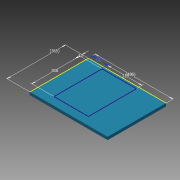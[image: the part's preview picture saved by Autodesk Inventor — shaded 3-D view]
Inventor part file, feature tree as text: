
AUTODESK INVENTOR PART (.ipt)
format: ipt  version: 2013 SP2 (Build 170200200, 200)  size: 77,312 bytes
history: native  units: mm
features: sketch x2, extrude x1
ambient origin geometry x8: Origin, YZ Plane, XZ Plane, XY Plane, X Axis, Y Axis, Z Axis, Center Point
bodies: Solid1 (feature_tree)
feature tree (3):
  extrude  "Extrusion1"  Depth=365.0mm
  sketch  "Sketch2"  dims[d2=18.0mm d3=0.0mm d4=300.0mm d6=215.0mm d7=15.0mm d8=100.0mm d9=486.0mm d10=365.0mm]
  sketch  "Sketch1"  dims[d0=486.0mm d1=365.0mm]
